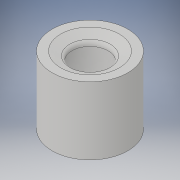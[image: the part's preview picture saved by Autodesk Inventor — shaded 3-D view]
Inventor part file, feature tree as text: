
AUTODESK INVENTOR PART (.ipt)
format: ipt  version: 2017 (Build 210142000, 142)  size: 151,040 bytes
history: native  units: in
note: dims shown in document units (in); Inventor stores cm internally (conversion verified against a paired STEP export)
features: revolve x1, sketch x1
ambient origin geometry x8: Origin, YZ Plane, XZ Plane, XY Plane, X Axis, Y Axis, Z Axis, Center Point
bodies: Solid1 (feature_tree)
feature tree (2):
  revolve  "Revolution1"  [1 undecoded]
  sketch  "Sketch1"  dims[d0=1.13in d1=3.75in d2=0.25in d3=0.1718in d5=1.0in d6=1.0in d7=90.0deg d8=0.5in d9=15.0deg d11=0.25in d12=1.25in d13=0.25in d15=0.25in d16=0.5in d17=0.5in d18=0.5in d19=2.5in d20=0.5in d22=0.375in d23=0.25in d25=0.234in d26=15.0deg d27=90.0deg]
note: 1 required parameter value undecoded (feature->parameter linkage not recoverable at this tier; creation-order binding heuristic only, values carry confidence <= 0.55)
